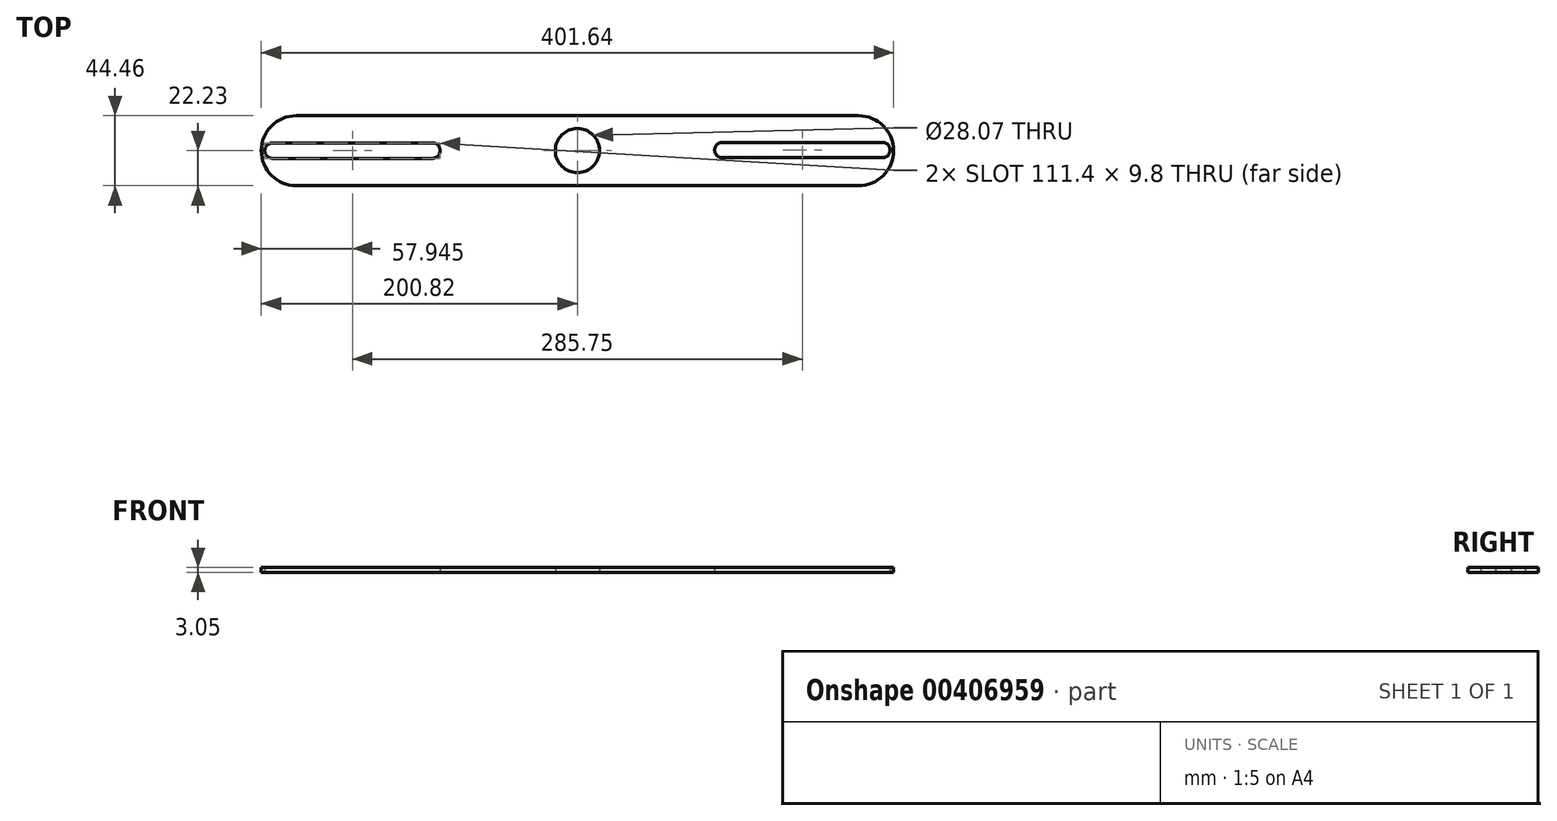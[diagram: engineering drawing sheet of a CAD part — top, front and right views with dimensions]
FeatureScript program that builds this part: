
annotation { "Feature Type Name" : "Feature", "Feature Type Description" : "" }
export const myFeature = defineFeature(function(context is Context, id is Id, definition is map)
    precondition{}
    {
        {
            var Q0;
            Q0=qCreatedBy(makeId("Top.planeOp"),FACE);
            var sketch = newSketch(context, id + "F0", { "sketchPlane" : qUnion([Q0])});
            skArc(sketch, "E0", {"start": v(178.6, -22.23) * mm, "mid": v(200.82, 0) * mm, "end": v(178.6, 22.22) * mm});
            skArc(sketch, "E1", {"start": v(-178.6, 22.22) * mm, "mid": v(-200.82, 0) * mm, "end": v(-178.6, -22.23) * mm});
            skLineSegment(sketch, "E2", {"start": v(-178.6, 22.22) * mm, "end": v(178.6, 22.22) * mm});
            skLineSegment(sketch, "E3", {"start": v(-178.6, -22.23) * mm, "end": v(178.6, -22.23) * mm});
            skCircle(sketch, "E4", {"center": v(0, 0) * mm, "radius": 14.03 * mm});
            skArc(sketch, "E5", {"start": v(-193.68, 4.9) * mm, "mid": v(-198.58, 0) * mm, "end": v(-193.68, -4.9) * mm});
            skArc(sketch, "E6", {"start": v(-92.08, -4.9) * mm, "mid": v(-87.17, 0) * mm, "end": v(-92.08, 4.9) * mm});
            skLineSegment(sketch, "E7", {"start": v(-193.68, 4.9) * mm, "end": v(-92.08, 4.9) * mm});
            skLineSegment(sketch, "E8", {"start": v(-193.68, -4.9) * mm, "end": v(-92.08, -4.9) * mm});
            skArc(sketch, "E9", {"start": v(92.08, 5.3) * mm, "mid": v(87.17, 0.4) * mm, "end": v(92.08, -4.5) * mm});
            skArc(sketch, "E10", {"start": v(193.68, -4.5) * mm, "mid": v(198.58, 0.4) * mm, "end": v(193.68, 5.3) * mm});
            skLineSegment(sketch, "E11", {"start": v(92.08, 5.3) * mm, "end": v(193.68, 5.3) * mm});
            skLineSegment(sketch, "E12", {"start": v(92.08, -4.5) * mm, "end": v(193.68, -4.5) * mm});
            skSolve(sketch);
        }
        {
            var Q0;
            {var subQ0=sQuery(id+"F0.wireOp",EDGE,"E0");Q0=makeQuery(id+"F0.imprint","IMPRINT",FACE,{"disambiguationData":[TD([[makeQuery(id+"F0.imprint","IMPRINT",EDGE,{"derivedFrom":subQ0}),1.0]])]});}
            extrude(context, id + "F1", {"entities" : qUnion([Q0]), "depth" : 3.05 * mm});
        }
    });
